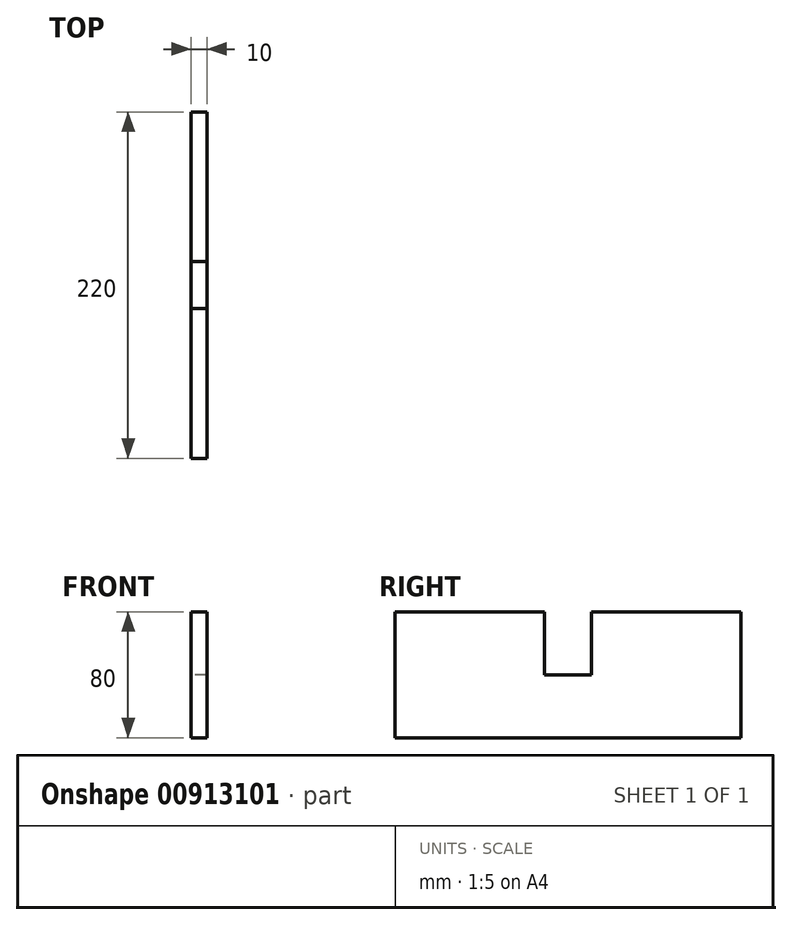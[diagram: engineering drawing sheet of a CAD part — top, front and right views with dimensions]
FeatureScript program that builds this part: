
annotation { "Feature Type Name" : "Feature", "Feature Type Description" : "" }
export const myFeature = defineFeature(function(context is Context, id is Id, definition is map)
    precondition{}
    {
        {
            var Q0;
            Q0=qCreatedBy(makeId("Right.planeOp"),FACE);
            var sketch = newSketch(context, id + "F0", { "sketchPlane" : qUnion([Q0])});
            skLineSegment(sketch, "E0.bottom", {"start": v(110, -40) * mm, "end": v(-110, -40) * mm});
            skLineSegment(sketch, "E0.left", {"start": v(110, -40) * mm, "end": v(110, 40) * mm});
            skLineSegment(sketch, "E0.right", {"start": v(-110, -40) * mm, "end": v(-110, 40) * mm});
            skPoint(sketch, "E0.middle", {"position": v(0, 0) * mm});
            skLineSegment(sketch, "E1", {"start": v(110, 40) * mm, "end": v(15, 40) * mm});
            skLineSegment(sketch, "E2.MirrorCS", {"start": v(-110, 40) * mm, "end": v(-15, 40) * mm});
            skLineSegment(sketch, "E3", {"start": v(-15, 40) * mm, "end": v(-15, 0) * mm});
            skLineSegment(sketch, "E4.MirrorCS", {"start": v(15, 40) * mm, "end": v(15, 0) * mm});
            skLineSegment(sketch, "E5", {"start": v(15, 0) * mm, "end": v(-15, 0) * mm});
            skPoint(sketch, "E6.orphan", {"position": v(15, 40) * mm});
            skSolve(sketch);
        }
        {
            var Q0;
            Q0 = qSketchRegion(id + "F0", true);
            extrude(context, id + "F1", {"entities" : qUnion([Q0]), "depth" : 10 * mm, "offsetDistance" : 25 * mm});
        }
    });
